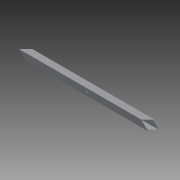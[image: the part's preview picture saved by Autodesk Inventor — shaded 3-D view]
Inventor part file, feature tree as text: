
AUTODESK INVENTOR PART (.ipt)
format: ipt  version: 2015 (Build 190159000, 159)  size: 121,344 bytes
history: native  units: in
note: dims shown in document units (in); Inventor stores cm internally (conversion verified against a paired STEP export)
features: sketch x4, projected_geometry x3, extrude x2, hole x2
ambient origin geometry x8: Origin, YZ Plane, XZ Plane, XY Plane, X Axis, Y Axis, Z Axis, Center Point
bodies: Solid1 (feature_tree)
feature tree (11):
  extrude  "Extrusion1"  Depth=1.0in
  hole  "Hole1"  [1 undecoded]
  extrude  "Extrusion2"  Depth=0.125in
  hole  "Hole2"  [1 undecoded]
  sketch  "Sketch1"  dims[d0=1.0in d1=1.0in]
  sketch  "Sketch2"  dims[d2=0.75in d3=0.75in]
  projected_geometry  "Projected Loop1"
  sketch  "Sketch3"  dims[d4=0.125in d5=0.125in]
  projected_geometry  "Projected Loop2"
  sketch  "Sketch4"  dims[d6=23.75in d7=0.0in d8=0.5in d9=0.5in d10=0.5in d11=0.5in d12=0.5in d13=11.875in d14=0.25in d15=0.75in d16=0.375in d17=0.25in d18=0.5635in d19=1.0in d20=0.8108in d21=0.625in d22=0.625in d23=0.625in d24=0.5in d25=0.0in d26=0.5in d27=1.5in d28=0.5in d29=1.5in d30=0.25in d31=0.75in d32=0.375in d33=0.25in d34=0.5635in d35=1.0in d36=0.8108in]
  projected_geometry  "Projected Loop3"
note: 2 required parameter values undecoded (feature->parameter linkage not recoverable at this tier; creation-order binding heuristic only, values carry confidence <= 0.55)
